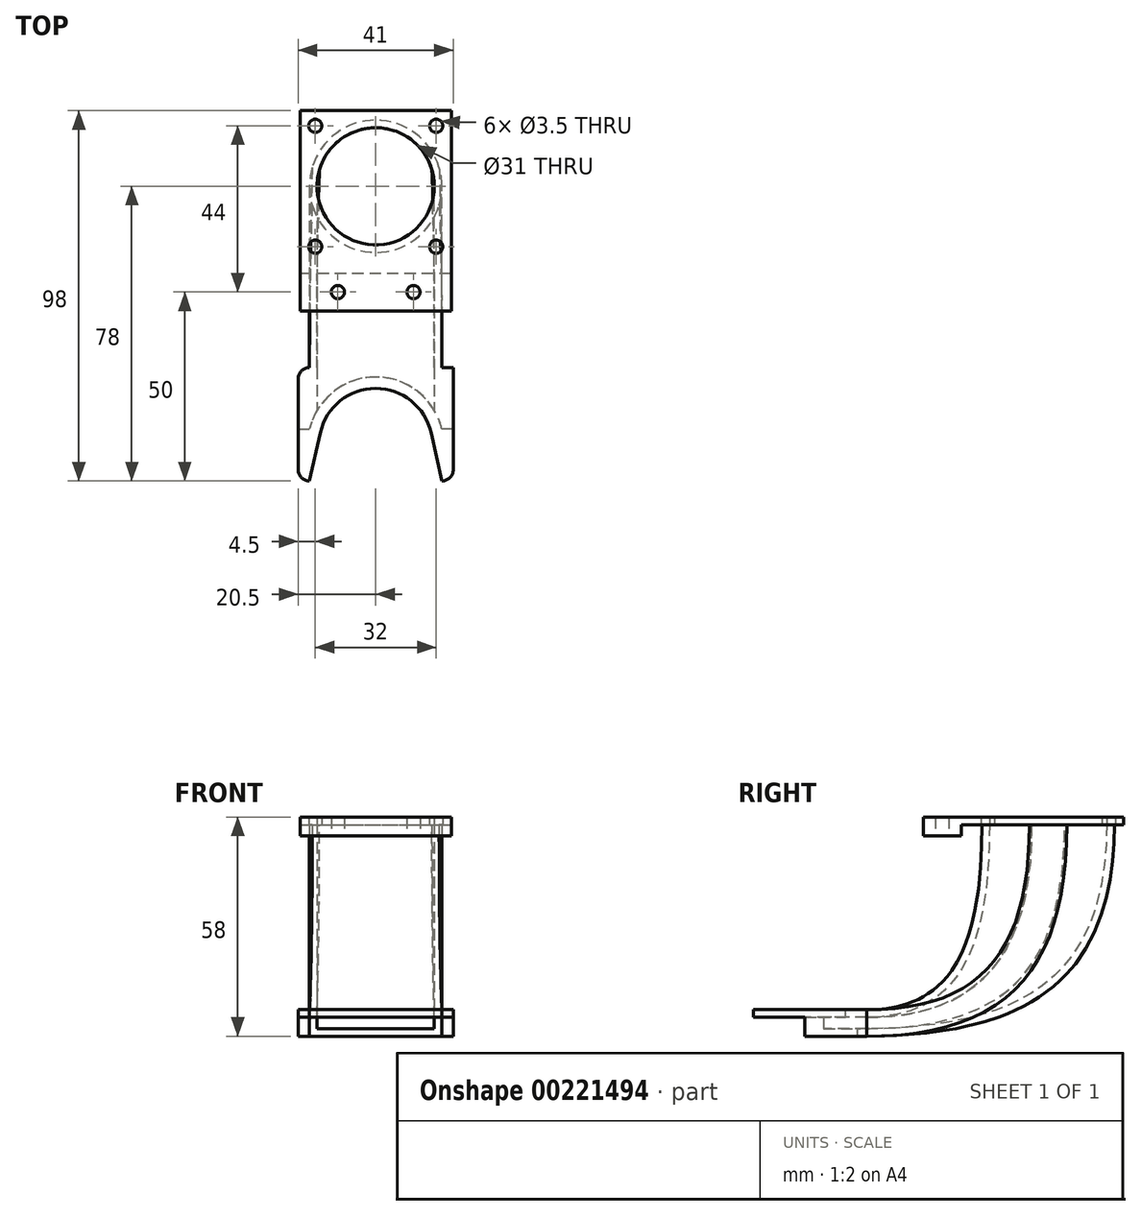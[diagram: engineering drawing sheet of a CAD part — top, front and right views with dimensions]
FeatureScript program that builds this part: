
annotation { "Feature Type Name" : "Feature", "Feature Type Description" : "" }
export const myFeature = defineFeature(function(context is Context, id is Id, definition is map)
    precondition{}
    {
        {
            var Q0;
            Q0=qCreatedBy(makeId("Top.planeOp"),FACE);
            var sketch = newSketch(context, id + "F0", { "sketchPlane" : qUnion([Q0])});
            skLineSegment(sketch, "E0.bottom", {"start": v(0, 0) * mm, "end": v(-40, 0) * mm});
            skLineSegment(sketch, "E0.top", {"start": v(0, 10) * mm, "end": v(-40, 10) * mm});
            skLineSegment(sketch, "E0.left", {"start": v(0, 0) * mm, "end": v(0, 10) * mm});
            skLineSegment(sketch, "E0.right", {"start": v(-40, 0) * mm, "end": v(-40, 10) * mm});
            skCircle(sketch, "E1", {"center": v(-30, 5) * mm, "radius": 1.75 * mm});
            skPoint(sketch, "E1.centerSnap0", {"position": v(-40, 5) * mm});
            skCircle(sketch, "E2", {"center": v(-10, 5) * mm, "radius": 1.75 * mm});
            skPoint(sketch, "E2.centerSnap0", {"position": v(0, 5) * mm});
            skSolve(sketch);
        }
        {
            var Q0;
            Q0=makeQuery(id+"F0.imprint","IMPRINT",FACE,{"disambiguationData":[TD([[makeQuery(id+"F0.imprint","IMPRINT",EDGE,{"derivedFrom":sQuery(id+"F0.wireOp",EDGE,"E0.bottom")}),-1.0]])]});
            extrude(context, id + "F1", {"entities" : qUnion([Q0]), "depth" : 5 * mm});
        }
        {
            var Q0;
            Q0=makeQuery(id+"F1.opExtrude","SWEPT_FACE",FACE,{"disambiguationData":[OSD([sQuery(id+"F0.wireOp",EDGE,"E0.top")])]});
            var sketch = newSketch(context, id + "F2", { "sketchPlane" : qUnion([Q0])});
            skLineSegment(sketch, "E3.bottom", {"start": v(40, 5) * mm, "end": v(0, 5) * mm});
            skLineSegment(sketch, "E3.top", {"start": v(40, 3) * mm, "end": v(0, 3) * mm});
            skLineSegment(sketch, "E3.left", {"start": v(40, 5) * mm, "end": v(40, 3) * mm});
            skLineSegment(sketch, "E3.right", {"start": v(0, 5) * mm, "end": v(0, 3) * mm});
            skSolve(sketch);
        }
        {
            var Q0;
            Q0=makeQuery(id+"F2.imprint","IMPRINT",FACE,{"disambiguationData":[TD([[makeQuery(id+"F2.imprint","IMPRINT",EDGE,{"derivedFrom":sQuery(id+"F2.wireOp",EDGE,"E3.bottom")}),-1.0]])]});
            extrude(context, id + "F3", {"entities" : qUnion([Q0]), "operationType" : NewBodyOperationType.ADD, "depth" : 43 * mm});
        }
        {
            var Q0;
            Q0=makeQuery(id+"F3.boolean.opBoolean","MERGE",FACE,{"derivedFrom":[makeQuery(id+"F1.opExtrude","CAP_FACE",FACE,{"disambiguationData":[OSD([sQuery(id+"F0.wireOp",EDGE,"E0.bottom"),sQuery(id+"F0.wireOp",EDGE,"E0.top"),sQuery(id+"F0.wireOp",EDGE,"E0.left"),sQuery(id+"F0.wireOp",EDGE,"E0.right"),sQuery(id+"F0.wireOp",EDGE,"E1"),sQuery(id+"F0.wireOp",EDGE,"E2")])],"isStart":false}),makeQuery(id+"F3.opExtrude","SWEPT_FACE",FACE,{"disambiguationData":[OSD([sQuery(id+"F2.wireOp",EDGE,"E3.bottom")])]})]});
            var sketch = newSketch(context, id + "F4", { "sketchPlane" : qUnion([Q0])});
            skLineSegment(sketch, "E4.bottom", {"start": v(-36, 49) * mm, "end": v(-4, 49) * mm, "construction": true});
            skLineSegment(sketch, "E4.top", {"start": v(-36, 17) * mm, "end": v(-4, 17) * mm, "construction": true});
            skLineSegment(sketch, "E4.left", {"start": v(-36, 49) * mm, "end": v(-36, 17) * mm, "construction": true});
            skLineSegment(sketch, "E4.right", {"start": v(-4, 49) * mm, "end": v(-4, 17) * mm, "construction": true});
            skPoint(sketch, "E5", {"position": v(-20, 49) * mm});
            skPoint(sketch, "E6", {"position": v(-36, 33) * mm});
            skSolve(sketch);
        }
        {
            var Q0;
            Q0=sQuery(id+"F4.wireOp",VERTEX,"E4.bottom.start");
            var Q1;
            Q1=sQuery(id+"F4.wireOp",VERTEX,"E4.left.end");
            var Q2;
            Q2=sQuery(id+"F4.wireOp",VERTEX,"E4.right.end");
            var Q3;
            Q3=sQuery(id+"F4.wireOp",VERTEX,"E4.right.start");
            var Q4;
            Q4=makeQuery(id+"F1.opExtrude","SWEPT_BODY",BODY,{"disambiguationData":[OSD([sQuery(id+"F0.wireOp",EDGE,"E0.bottom"),sQuery(id+"F0.wireOp",EDGE,"E0.top"),sQuery(id+"F0.wireOp",EDGE,"E0.left"),sQuery(id+"F0.wireOp",EDGE,"E0.right"),sQuery(id+"F0.wireOp",EDGE,"E1"),sQuery(id+"F0.wireOp",EDGE,"E2")])]});
            hole(context, id + "F5", {"style" : HoleStyle.SIMPLE, "endStyle" : HoleEndStyle.THROUGH, "holeDiameter" : 3.5 * mm, "tappedDepth" : 12 * mm, "tapClearance" : 3, "locations" : qUnion([Q0, Q1, Q2, Q3]), "scope" : qUnion([Q4])});
        }
        {
            var Q0;
            Q0=makeQuery(id+"F3.boolean.opBoolean","MERGE",FACE,{"derivedFrom":[makeQuery(id+"F1.opExtrude","CAP_FACE",FACE,{"disambiguationData":[OSD([sQuery(id+"F0.wireOp",EDGE,"E0.bottom"),sQuery(id+"F0.wireOp",EDGE,"E0.top"),sQuery(id+"F0.wireOp",EDGE,"E0.left"),sQuery(id+"F0.wireOp",EDGE,"E0.right"),sQuery(id+"F0.wireOp",EDGE,"E1"),sQuery(id+"F0.wireOp",EDGE,"E2")])],"isStart":false}),makeQuery(id+"F3.opExtrude","SWEPT_FACE",FACE,{"disambiguationData":[OSD([sQuery(id+"F2.wireOp",EDGE,"E3.bottom")])]})]});
            var sketch = newSketch(context, id + "F6", { "sketchPlane" : qUnion([Q0])});
            skCircle(sketch, "E7", {"center": v(-20, 33) * mm, "radius": 17.5 * mm});
            skLineSegment(sketch, "E8", {"start": v(-36, 17) * mm, "end": v(-36, 49) * mm, "construction": true});
            skPoint(sketch, "E9", {"position": v(-36, 33) * mm});
            skSolve(sketch);
        }
        {
            var Q0;
            Q0=makeQuery(id+"F6.imprint","IMPRINT",FACE,{"disambiguationData":[TD([[makeQuery(id+"F6.imprint","IMPRINT",EDGE,{"derivedFrom":sQuery(id+"F6.wireOp",EDGE,"E7")}),1.0]])]});
            extrude(context, id + "F7", {"entities" : qUnion([Q0]), "operationType" : NewBodyOperationType.REMOVE, "endBound" : BoundingType.THROUGH_ALL, "oppositeDirection" : true, "depth" : 25 * mm});
        }
        {
            var Q0;
            Q0=makeQuery(id+"F3.opExtrude","SWEPT_FACE",FACE,{"disambiguationData":[OSD([sQuery(id+"F2.wireOp",EDGE,"E3.top")])]});
            var sketch = newSketch(context, id + "F8", { "sketchPlane" : qUnion([Q0])});
            skSolve(sketch);
        }
        {
            var Q0;
            Q0=makeQuery(id+"F1.opExtrude","SWEPT_FACE",FACE,{"disambiguationData":[OSD([sQuery(id+"F0.wireOp",EDGE,"E0.bottom")])]});
            cPlane(context, id + "F9", {"entities" : qUnion([Q0]), "cplaneType" : CPlaneType.OFFSET, "offset" : 45 * mm, "width" : 150 * mm, "height" : 150 * mm});
        }
        {
            var Q0;
            Q0=qCreatedBy(id+"F9.planeOp",FACE);
            var sketch = newSketch(context, id + "F10", { "sketchPlane" : qUnion([Q0])});
            skLineSegment(sketch, "E10.bottom", {"start": v(-37.5, -53) * mm, "end": v(-2.5, -53) * mm});
            skLineSegment(sketch, "E10.top", {"start": v(-37.5, -46) * mm, "end": v(-2.5, -46) * mm});
            skLineSegment(sketch, "E10.left", {"start": v(-37.5, -53) * mm, "end": v(-37.5, -46) * mm});
            skLineSegment(sketch, "E10.right", {"start": v(-2.5, -53) * mm, "end": v(-2.5, -46) * mm});
            skPoint(sketch, "E11", {"position": v(-20, -46) * mm});
            skSolve(sketch);
        }
        {
            var Q0;
            Q0=makeQuery(id+"F10.imprint","IMPRINT",FACE,{"disambiguationData":[TD([[makeQuery(id+"F10.imprint","IMPRINT",EDGE,{"derivedFrom":sQuery(id+"F10.wireOp",EDGE,"E10.bottom")}),1.0]])]});
            extrude(context, id + "F11", {"entities" : qUnion([Q0]), "oppositeDirection" : true, "depth" : 30 * mm});
        }
        {
            var Q0;
            {var subQ0=sQuery(id+"F2.wireOp",EDGE,"E3.top");Q0=makeQuery(id+"F8.imprint","IMPRINT",FACE,{"disambiguationData":[TD([[makeQuery(id+"F8.imprint","IMPRINT",EDGE,{"derivedFrom":makeQuery(id+"F3.opExtrude","CAP_EDGE",EDGE,{"disambiguationData":[OSD([subQ0])],"isStart":false})}),1.0]])]});}
            var sketch = newSketch(context, id + "F12", { "sketchPlane" : qUnion([Q0])});
            skArc(sketch, "E12", {"start": v(-3.21, -28.05) * mm, "mid": v(-20, -15.5) * mm, "end": v(-36.79, -28.05) * mm});
            skArc(sketch, "E13", {"start": v(-36.79, -37.95) * mm, "mid": v(-20, -50.5) * mm, "end": v(-3.21, -37.95) * mm});
            skArc(sketch, "E14", {"start": v(-36.79, -28.05) * mm, "mid": v(-37.5, -33) * mm, "end": v(-36.79, -37.95) * mm});
            skArc(sketch, "E15", {"start": v(-3.21, -37.95) * mm, "mid": v(-2.5, -33) * mm, "end": v(-3.21, -28.05) * mm});
            skLineSegment(sketch, "E16", {"start": v(-36.79, -28.05) * mm, "end": v(-3.21, -37.95) * mm, "construction": true});
            skLineSegment(sketch, "E17", {"start": v(-3.21, -28.05) * mm, "end": v(-36.79, -37.95) * mm, "construction": true});
            skLineSegment(sketch, "E18", {"start": v(-2.5, -33) * mm, "end": v(-37.5, -33) * mm, "construction": true});
            skSolve(sketch);
        }
        {
            var Q1;
            Q1 = qSketchRegion(id + "F12", true);
            var Q2;
            Q2=makeQuery(id+"F11.opExtrude","CAP_FACE",FACE,{"disambiguationData":[OSD([sQuery(id+"F10.wireOp",EDGE,"E10.bottom"),sQuery(id+"F10.wireOp",EDGE,"E10.top"),sQuery(id+"F10.wireOp",EDGE,"E10.left"),sQuery(id+"F10.wireOp",EDGE,"E10.right")])],"isStart":false});
            var Q3;
            Q3=sQuery(id+"FFYjmbXSwY1wBhW_2.wireOp",VERTEX,"5CUcN9Ah-aoQc-i0Y4-lSSF-3NxKRFAfKakx.start");
            var Q4;
            Q4=sQuery(id+"FFYjmbXSwY1wBhW_2.wireOp",VERTEX,"9UqwaanU-PZ8O-Q84W-1Uu3-IYepP7ym5t6i.end");
            var Q5;
            Q5=sQuery(id+"FFYjmbXSwY1wBhW_2.wireOp",VERTEX,"3rHOv9Gl-2p6t-3ORE-IPYh-5aPjCGt6IKt6.end");
            var Q6;
            Q6=sQuery(id+"FFYjmbXSwY1wBhW_2.wireOp",VERTEX,"h81LCoKd-EBxs-FelB-gbCS-DPIwCHQTHsDM.start");
            loft(context, id + "F13", {"operationType" : NewBodyOperationType.ADD, "startCondition" : LoftEndDerivativeType.NORMAL_TO_PROFILE, "startMagnitude" : 2, "endCondition" : LoftEndDerivativeType.NORMAL_TO_PROFILE, "endMagnitude" : 2, "sheetProfilesArray" : [{ "sheetProfileEntities" : qUnion([Q1]) }, { "sheetProfileEntities" : qUnion([Q2]) }], "connections" : [{ "connectionEntities" : qUnion([Q3, Q4, Q5, Q6]), "connectionEdgeQueries" : qUnion([]), "connectionEdgeParameters" : [] }]});
        }
        {
            var Q0;
            Q0=makeQuery(id+"F13.opLoft","CAP_FACE",FACE,{"disambiguationData":[OSD([makeQuery(id+"F12.imprint","IMPRINT",FACE,{"disambiguationData":[TD([[makeQuery(id+"F12.imprint","IMPRINT",EDGE,{"derivedFrom":sQuery(id+"F12.wireOp",EDGE,"E12")}),1.0]])]})])],"isStart":true});
            shell(context, id + "F14", {"entities" : qUnion([Q0]), "thickness" : 2 * mm});
        }
        {
            var Q0;
            Q0=makeQuery(id+"F11.opExtrude","SWEPT_FACE",FACE,{"disambiguationData":[OSD([sQuery(id+"F10.wireOp",EDGE,"E10.top")])]});
            var sketch = newSketch(context, id + "F15", { "sketchPlane" : qUnion([Q0])});
            skArc(sketch, "E19", {"start": v(-5.36, -32.22) * mm, "mid": v(-20, -20.5) * mm, "end": v(-34.64, -32.22) * mm});
            skPoint(sketch, "E19.centerSnap0", {"position": v(-20, -45) * mm});
            skLineSegment(sketch, "E20", {"start": v(-2.5, -45) * mm, "end": v(-5.36, -32.22) * mm});
            skLineSegment(sketch, "E21", {"start": v(-37.5, -45) * mm, "end": v(-34.64, -32.22) * mm});
            skLineSegment(sketch, "E22", {"start": v(-37.5, -45) * mm, "end": v(-2.5, -45) * mm});
            skSolve(sketch);
        }
        {
            var Q0;
            Q0=makeQuery(id+"F15.imprint","IMPRINT",FACE,{"disambiguationData":[TD([[makeQuery(id+"F15.imprint","IMPRINT",EDGE,{"derivedFrom":sQuery(id+"F15.wireOp",EDGE,"E19")}),1.0]])]});
            extrude(context, id + "F16", {"entities" : qUnion([Q0]), "operationType" : NewBodyOperationType.REMOVE, "endBound" : BoundingType.THROUGH_ALL, "oppositeDirection" : true, "depth" : 25 * mm});
        }
        {
            var Q0;
            Q0=makeQuery(id+"F11.opExtrude","SWEPT_FACE",FACE,{"disambiguationData":[OSD([sQuery(id+"F10.wireOp",EDGE,"E10.bottom")])]});
            var sketch = newSketch(context, id + "F17", { "sketchPlane" : qUnion([Q0])});
            skArc(sketch, "E23", {"start": v(-37.5, 31.29) * mm, "mid": v(-20, 17.5) * mm, "end": v(-2.5, 31.29) * mm});
            skLineSegment(sketch, "E24", {"start": v(-37.5, 45) * mm, "end": v(-37.5, 31.29) * mm});
            skPoint(sketch, "E24.endSnap0", {"position": v(-37.5, 30) * mm});
            skLineSegment(sketch, "E25", {"start": v(-2.5, 45) * mm, "end": v(-2.5, 31.29) * mm});
            skLineSegment(sketch, "E26", {"start": v(-2.5, 45) * mm, "end": v(-37.5, 45) * mm});
            skSolve(sketch);
        }
        {
            var Q0;
            {var subQ1=sQuery(id+"F10.wireOp",EDGE,"E10.bottom");var subQ2=makeQuery(id+"F11.opExtrude","SWEPT_FACE",FACE,{"disambiguationData":[OSD([subQ1])]});var subQ6=makeQuery(id+"F16.opExtrude","SWEPT_FACE",FACE,{"disambiguationData":[OSD([sQuery(id+"F15.wireOp",EDGE,"E19")])]});var subQ12=makeQuery(id+"F16.boolean.opBoolean","INTERSECT",EDGE,{"derivedFrom":[subQ2,subQ6]});Q0=makeQuery(id+"F17.imprint","IMPRINT",FACE,{"disambiguationData":[TD([[makeQuery(id+"F17.imprint","IMPRINT",EDGE,{"derivedFrom":subQ12}),-1.0]])]});}
            var Q1;
            Q1=makeQuery(id+"F14.opShell","OFFSET_FACE",FACE,{"disambiguationData":[OSD([sQuery(id+"F10.wireOp",EDGE,"E10.top")])]});
            extrude(context, id + "F18", {"entities" : qUnion([Q0]), "operationType" : NewBodyOperationType.REMOVE, "endBound" : BoundingType.UP_TO_SURFACE, "oppositeDirection" : true, "endBoundEntityFace" : qUnion([Q1]), "depth" : 25 * mm});
        }
        {
            var Q0;
            Q0=makeQuery(id+"F8.imprint","IMPRINT",FACE,{"disambiguationData":[TD([[makeQuery(id+"F8.imprint","IMPRINT",EDGE,{"derivedFrom":makeQuery(id+"F7.boolean.opBoolean","INTERSECT",EDGE,{"derivedFrom":[makeQuery(id+"F3.opExtrude","SWEPT_FACE",FACE,{"disambiguationData":[OSD([sQuery(id+"F2.wireOp",EDGE,"E3.top")])]}),makeQuery(id+"F7.opExtrude","SWEPT_FACE",FACE,{"disambiguationData":[OSD([sQuery(id+"F6.wireOp",EDGE,"E7")])]})]})}),1.0]])]});
            var sketch = newSketch(context, id + "F19", { "sketchPlane" : qUnion([Q0])});
            skCircle(sketch, "E27", {"center": v(-20, -33) * mm, "radius": 17.5 * mm});
            skCircle(sketch, "E28", {"center": v(-20, -33) * mm, "radius": 15.5 * mm});
            skSolve(sketch);
        }
        {
            var Q0;
            Q0=makeQuery(id+"F19.imprint","IMPRINT",FACE,{"disambiguationData":[TD([[makeQuery(id+"F19.imprint","IMPRINT",EDGE,{"derivedFrom":sQuery(id+"F19.wireOp",EDGE,"E27")}),1.0]])]});
            var Q1;
            Q1=makeQuery(id+"F3.boolean.opBoolean","MERGE",FACE,{"derivedFrom":[makeQuery(id+"F1.opExtrude","CAP_FACE",FACE,{"disambiguationData":[OSD([sQuery(id+"F0.wireOp",EDGE,"E0.bottom"),sQuery(id+"F0.wireOp",EDGE,"E0.top"),sQuery(id+"F0.wireOp",EDGE,"E0.left"),sQuery(id+"F0.wireOp",EDGE,"E0.right"),sQuery(id+"F0.wireOp",EDGE,"E1"),sQuery(id+"F0.wireOp",EDGE,"E2")])],"isStart":false}),makeQuery(id+"F3.opExtrude","SWEPT_FACE",FACE,{"disambiguationData":[OSD([sQuery(id+"F2.wireOp",EDGE,"E3.bottom")])]})]});
            extrude(context, id + "F20", {"entities" : qUnion([Q0]), "operationType" : NewBodyOperationType.ADD, "endBound" : BoundingType.UP_TO_SURFACE, "oppositeDirection" : true, "endBoundEntityFace" : qUnion([Q1]), "depth" : 25 * mm});
        }
        {
            var Q0;
            Q0=makeQuery(id+"F11.opExtrude","SWEPT_FACE",FACE,{"disambiguationData":[OSD([sQuery(id+"F10.wireOp",EDGE,"E10.left")])]});
            var sketch = newSketch(context, id + "F24", { "sketchPlane" : qUnion([Q0])});
            skLineSegment(sketch, "E29.bottom", {"start": v(15, -46) * mm, "end": v(45, -46) * mm});
            skLineSegment(sketch, "E29.top", {"start": v(15, -53) * mm, "end": v(45, -53) * mm});
            skLineSegment(sketch, "E29.left", {"start": v(15, -46) * mm, "end": v(15, -53) * mm});
            skLineSegment(sketch, "E29.right", {"start": v(45, -46) * mm, "end": v(45, -53) * mm});
            skSolve(sketch);
        }
        {
            var Q0;
            {var subQ1=sQuery(id+"F17.wireOp",EDGE,"E24");var subQ5=makeQuery(id+"F18.boolean.opBoolean","COPY",EDGE,{"derivedFrom":makeQuery(id+"F18.opExtrude","TWEAK_EDGE",EDGE,{"derivedFrom":[makeQuery(id+"F14.opShell","OFFSET_FACE",FACE,{"disambiguationData":[OSD([sQuery(id+"F10.wireOp",EDGE,"E10.top")])]}),makeQuery(id+"F17.imprint","IMPRINT",EDGE,{"derivedFrom":subQ1})]})});Q0=makeQuery(id+"F24.imprint","IMPRINT",FACE,{"disambiguationData":[TD([[makeQuery(id+"F24.imprint","IMPRINT",EDGE,{"derivedFrom":subQ5}),1.0]])]});}
            var Q1;
            {var subQ2=sQuery(id+"F24.wireOp",EDGE,"E29.bottom");Q1=makeQuery(id+"F24.imprint","IMPRINT",FACE,{"disambiguationData":[TD([[makeQuery(id+"F24.imprint","IMPRINT",EDGE,{"derivedFrom":subQ2}),-1.0]])]});}
            extrude(context, id + "F21", {"entities" : qUnion([Q0, Q1]), "operationType" : NewBodyOperationType.ADD, "depth" : 3 * mm});
        }
        {
            var Q0;
            Q0=makeQuery(id+"F11.opExtrude","SWEPT_FACE",FACE,{"disambiguationData":[OSD([sQuery(id+"F10.wireOp",EDGE,"E10.right")])]});
            var sketch = newSketch(context, id + "F22", { "sketchPlane" : qUnion([Q0])});
            skLineSegment(sketch, "E30.bottom", {"start": v(-15, -53) * mm, "end": v(-45, -53) * mm});
            skLineSegment(sketch, "E30.top", {"start": v(-15, -46) * mm, "end": v(-45, -46) * mm});
            skLineSegment(sketch, "E30.left", {"start": v(-15, -53) * mm, "end": v(-15, -46) * mm});
            skLineSegment(sketch, "E30.right", {"start": v(-45, -53) * mm, "end": v(-45, -46) * mm});
            skSolve(sketch);
        }
        {
            var Q0;
            {var subQ1=sQuery(id+"F22.wireOp",EDGE,"E30.top");Q0=makeQuery(id+"F22.imprint","IMPRINT",FACE,{"disambiguationData":[TD([[makeQuery(id+"F22.imprint","IMPRINT",EDGE,{"derivedFrom":subQ1}),1.0]])]});}
            var Q1;
            {var subQ1=sQuery(id+"F17.wireOp",EDGE,"E25");var subQ5=makeQuery(id+"F18.boolean.opBoolean","COPY",EDGE,{"derivedFrom":makeQuery(id+"F18.opExtrude","TWEAK_EDGE",EDGE,{"derivedFrom":[makeQuery(id+"F14.opShell","OFFSET_FACE",FACE,{"disambiguationData":[OSD([sQuery(id+"F10.wireOp",EDGE,"E10.top")])]}),makeQuery(id+"F17.imprint","IMPRINT",EDGE,{"derivedFrom":subQ1})]})});Q1=makeQuery(id+"F22.imprint","IMPRINT",FACE,{"disambiguationData":[TD([[makeQuery(id+"F22.imprint","IMPRINT",EDGE,{"derivedFrom":subQ5}),-1.0]])]});}
            extrude(context, id + "F23", {"entities" : qUnion([Q0, Q1]), "operationType" : NewBodyOperationType.ADD, "depth" : 3 * mm});
        }
        {
            var Q0;
            Q0=makeQuery(id+"F23.opExtrude","CAP_EDGE",EDGE,{"disambiguationData":[OSD([sQuery(id+"F22.wireOp",EDGE,"E30.right")])],"isStart":false});
            var Q1;
            Q1=makeQuery(id+"F21.opExtrude","CAP_EDGE",EDGE,{"disambiguationData":[OSD([sQuery(id+"F24.wireOp",EDGE,"E29.right")])],"isStart":false});
            var Q2;
            Q2=makeQuery(id+"F21.opExtrude","CAP_EDGE",EDGE,{"disambiguationData":[OSD([sQuery(id+"F24.wireOp",EDGE,"E29.left")])],"isStart":false});
            fillet(context, id + "F25", {"entities" : qUnion([Q0, Q1, Q2]), "radius" : 3 * mm, "tangentPropagation" : true, "allowEdgeOverflow" : false});
        }
    });
